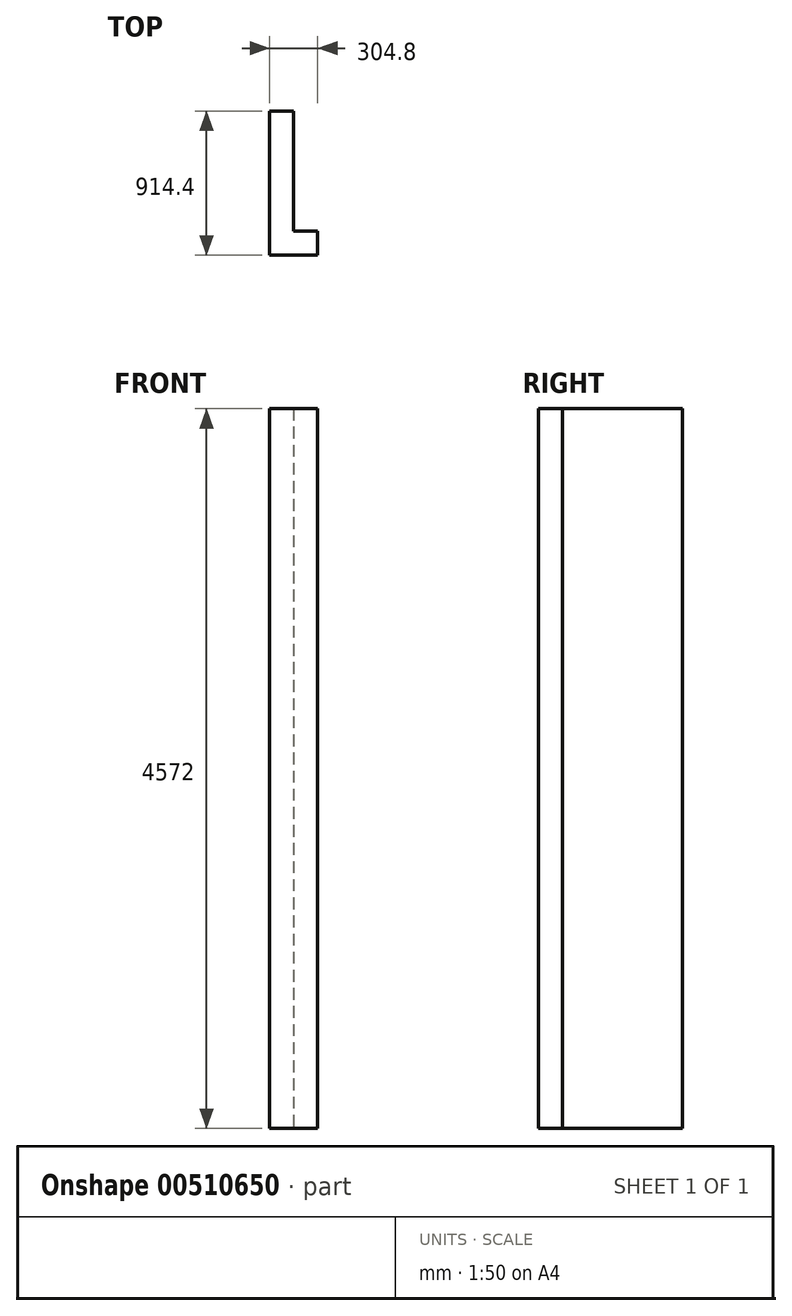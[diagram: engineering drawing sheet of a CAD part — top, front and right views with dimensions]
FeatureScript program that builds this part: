
annotation { "Feature Type Name" : "Feature", "Feature Type Description" : "" }
export const myFeature = defineFeature(function(context is Context, id is Id, definition is map)
    precondition{}
    {
        {
            var Q0;
            Q0=qCreatedBy(makeId("Top.planeOp"),FACE);
            var sketch = newSketch(context, id + "F0", { "sketchPlane" : qUnion([Q0])});
            skLineSegment(sketch, "E0", {"start": v(-255.85, 489) * mm, "end": v(-255.85, -425.4) * mm});
            skLineSegment(sketch, "E1", {"start": v(-255.85, -425.4) * mm, "end": v(48.95, -425.4) * mm});
            skLineSegment(sketch, "E2", {"start": v(-255.85, 489) * mm, "end": v(-103.45, 489) * mm});
            skLineSegment(sketch, "E3", {"start": v(-103.45, 489) * mm, "end": v(-103.45, -273) * mm});
            skLineSegment(sketch, "E4", {"start": v(48.95, -425.4) * mm, "end": v(48.95, -273) * mm});
            skLineSegment(sketch, "E5", {"start": v(48.95, -273) * mm, "end": v(-103.45, -273) * mm});
            skSolve(sketch);
        }
        {
            var Q0;
            Q0 = qSketchRegion(id + "F0", true);
            extrude(context, id + "F1", {"entities" : qUnion([Q0]), "depth" : 4572 * mm, "offsetDistance" : 30.48 * mm});
        }
    });
